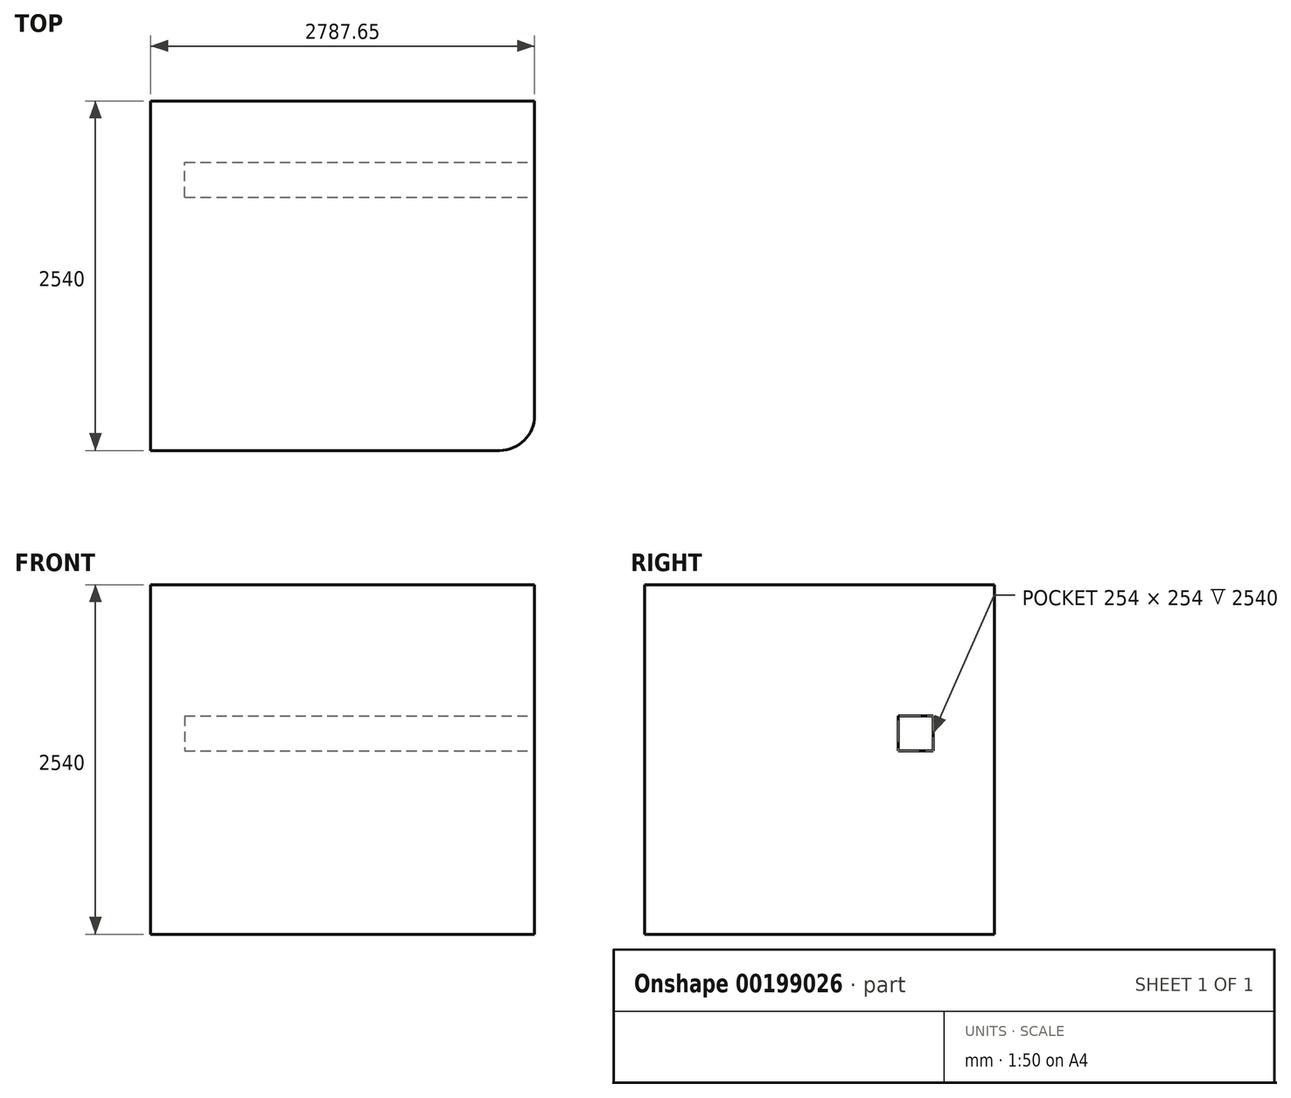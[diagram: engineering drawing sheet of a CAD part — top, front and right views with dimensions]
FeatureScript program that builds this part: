
annotation { "Feature Type Name" : "Feature", "Feature Type Description" : "" }
export const myFeature = defineFeature(function(context is Context, id is Id, definition is map)
    precondition{}
    {
        {
            var Q0;
            Q0=qCreatedBy(makeId("Top.planeOp"),FACE);
            var sketch = newSketch(context, id + "F0", { "sketchPlane" : qUnion([Q0])});
            skLineSegment(sketch, "E0.bottom", {"start": v(-1523.33, 753.9) * mm, "end": v(1264.32, 753.9) * mm});
            skLineSegment(sketch, "E0.top", {"start": v(-1523.33, -1786.1) * mm, "end": v(1010.32, -1786.1) * mm});
            skLineSegment(sketch, "E0.left", {"start": v(-1523.33, 753.9) * mm, "end": v(-1523.33, -1786.1) * mm});
            skLineSegment(sketch, "E0.right", {"start": v(1264.32, 753.9) * mm, "end": v(1264.32, -1532.1) * mm});
            skPoint(sketch, "E1.visualSharp", {"position": v(1264.32, -1786.1) * mm});
            skArc(sketch, "E1.filletArc", {"start": v(1010.32, -1786.1) * mm, "mid": v(1189.92, -1711.7) * mm, "end": v(1264.32, -1532.1) * mm});
            skSolve(sketch);
        }
        {
            var Q0;
            Q0=makeQuery(id+"F0.imprint","IMPRINT",FACE,{"disambiguationData":[TD([[makeQuery(id+"F0.imprint","IMPRINT",EDGE,{"derivedFrom":sQuery(id+"F0.wireOp",EDGE,"E0.bottom")}),-1.0]])]});
            extrude(context, id + "F1", {"entities" : qUnion([Q0]), "depth" : 2540 * mm});
        }
        {
            var Q0;
            Q0=makeQuery(id+"F1.opExtrude","SWEPT_FACE",FACE,{"disambiguationData":[OSD([sQuery(id+"F0.wireOp",EDGE,"E0.right")])]});
            var sketch = newSketch(context, id + "F2", { "sketchPlane" : qUnion([Q0])});
            skLineSegment(sketch, "E2.bottom", {"start": v(55.4, 1587.5) * mm, "end": v(309.4, 1587.5) * mm});
            skLineSegment(sketch, "E2.top", {"start": v(55.4, 1333.5) * mm, "end": v(309.4, 1333.5) * mm});
            skLineSegment(sketch, "E2.left", {"start": v(55.4, 1587.5) * mm, "end": v(55.4, 1333.5) * mm});
            skLineSegment(sketch, "E2.right", {"start": v(309.4, 1587.5) * mm, "end": v(309.4, 1333.5) * mm});
            skSolve(sketch);
        }
        {
            var Q0;
            Q0 = qSketchRegion(id + "F2", true);
            extrude(context, id + "F3", {"entities" : qUnion([Q0]), "operationType" : NewBodyOperationType.REMOVE, "oppositeDirection" : true, "depth" : 2540 * mm});
        }
    });
